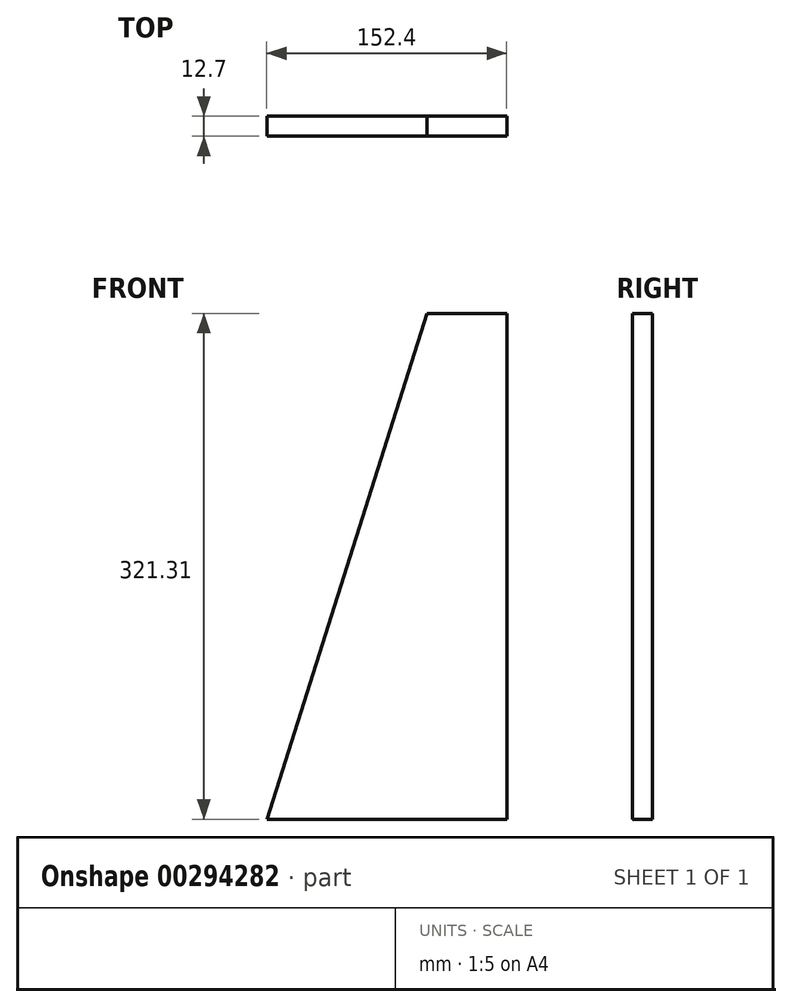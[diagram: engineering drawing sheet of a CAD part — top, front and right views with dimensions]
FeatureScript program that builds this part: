
annotation { "Feature Type Name" : "Feature", "Feature Type Description" : "" }
export const myFeature = defineFeature(function(context is Context, id is Id, definition is map)
    precondition{}
    {
        {
            var Q0;
            Q0=qCreatedBy(makeId("Front.planeOp"),FACE);
            var sketch = newSketch(context, id + "F0", { "sketchPlane" : qUnion([Q0])});
            skLineSegment(sketch, "E0", {"start": v(-88.38, -82.71) * mm, "end": v(64.02, -82.71) * mm});
            skLineSegment(sketch, "E1", {"start": v(64.02, -82.71) * mm, "end": v(64.02, 238.6) * mm});
            skLineSegment(sketch, "E2", {"start": v(64.02, 238.6) * mm, "end": v(13.22, 238.6) * mm});
            skLineSegment(sketch, "E3", {"start": v(13.22, 238.6) * mm, "end": v(-88.38, -82.71) * mm});
            skSolve(sketch);
        }
        {
            var Q0;
            Q0=makeQuery(id+"F0.imprint","IMPRINT",FACE,{"disambiguationData":[TD([[makeQuery(id+"F0.imprint","IMPRINT",EDGE,{"derivedFrom":sQuery(id+"F0.wireOp",EDGE,"E0")}),1.0]])]});
            extrude(context, id + "F1", {"entities" : qUnion([Q0]), "depth" : 12.7 * mm});
        }
    });
